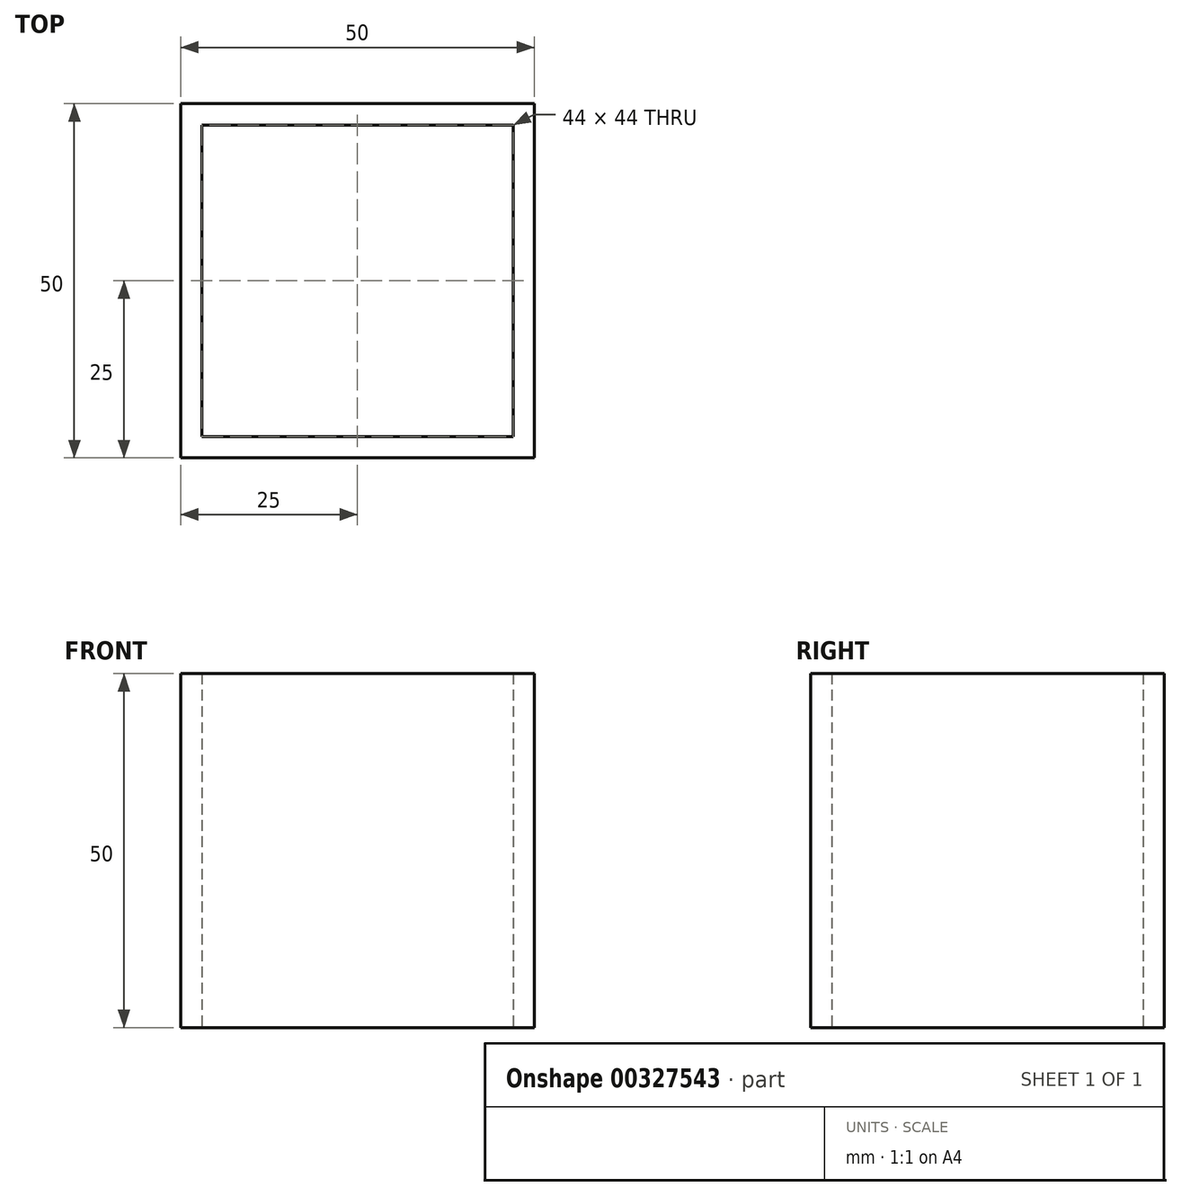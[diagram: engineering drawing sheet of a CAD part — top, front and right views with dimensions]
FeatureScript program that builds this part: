
annotation { "Feature Type Name" : "Feature", "Feature Type Description" : "" }
export const myFeature = defineFeature(function(context is Context, id is Id, definition is map)
    precondition{}
    {
        {
            var Q0;
            Q0=qCreatedBy(makeId("Top.planeOp"),FACE);
            var sketch = newSketch(context, id + "F0", { "sketchPlane" : qUnion([Q0])});
            skLineSegment(sketch, "E0.bottom", {"start": v(-25, 25) * mm, "end": v(25, 25) * mm});
            skLineSegment(sketch, "E0.top", {"start": v(-25, -25) * mm, "end": v(25, -25) * mm});
            skLineSegment(sketch, "E0.left", {"start": v(-25, 25) * mm, "end": v(-25, -25) * mm});
            skLineSegment(sketch, "E0.right", {"start": v(25, 25) * mm, "end": v(25, -25) * mm});
            skPoint(sketch, "E0.middle", {"position": v(0, 0) * mm});
            skLineSegment(sketch, "E1.bottom", {"start": v(-22, 22) * mm, "end": v(22, 22) * mm});
            skLineSegment(sketch, "E1.top", {"start": v(-22, -22) * mm, "end": v(22, -22) * mm});
            skLineSegment(sketch, "E1.left", {"start": v(-22, 22) * mm, "end": v(-22, -22) * mm});
            skLineSegment(sketch, "E1.right", {"start": v(22, 22) * mm, "end": v(22, -22) * mm});
            skSolve(sketch);
        }
        {
            var Q0;
            Q0=makeQuery(id+"F0.imprint","IMPRINT",FACE,{"disambiguationData":[TD([[makeQuery(id+"F0.imprint","IMPRINT",EDGE,{"derivedFrom":sQuery(id+"F0.wireOp",EDGE,"E0.bottom")}),-1.0]])]});
            extrude(context, id + "F1", {"entities" : qUnion([Q0]), "depth" : 50 * mm, "symmetric" : true});
        }
    });
